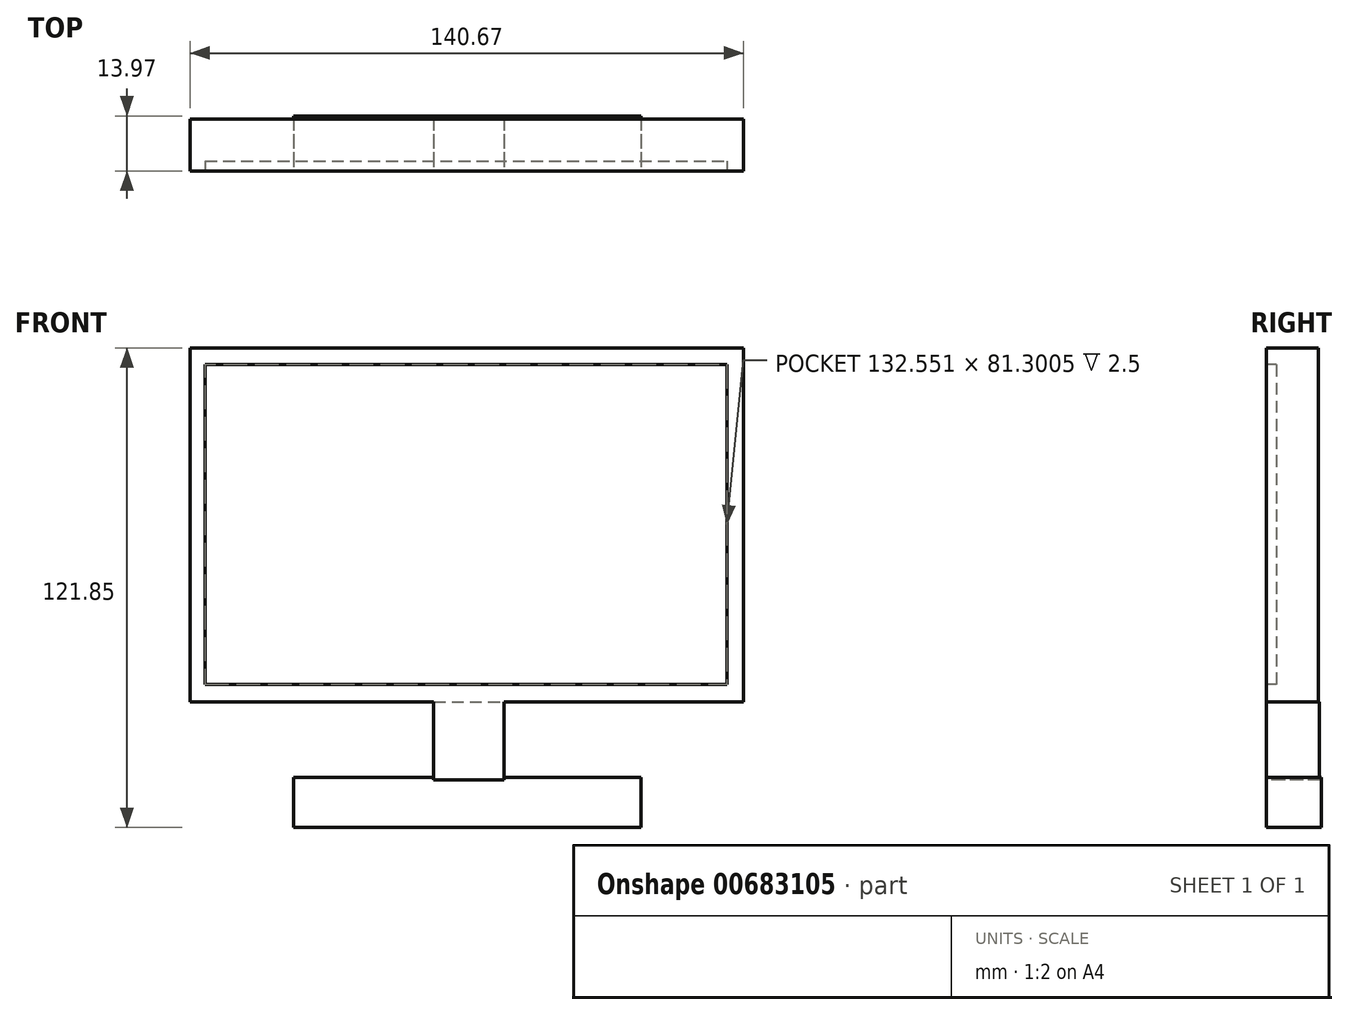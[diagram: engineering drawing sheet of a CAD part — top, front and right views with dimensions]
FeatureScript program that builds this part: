
annotation { "Feature Type Name" : "Feature", "Feature Type Description" : "" }
export const myFeature = defineFeature(function(context is Context, id is Id, definition is map)
    precondition{}
    {
        {
            var Q0;
            Q0=qCreatedBy(makeId("Front.planeOp"),FACE);
            var sketch = newSketch(context, id + "F0", { "sketchPlane" : qUnion([Q0])});
            skLineSegment(sketch, "E0.bottom", {"start": v(-71.8, 53.92) * mm, "end": v(68.86, 53.92) * mm});
            skLineSegment(sketch, "E0.top", {"start": v(-71.8, -36.04) * mm, "end": v(68.86, -36.04) * mm});
            skLineSegment(sketch, "E0.left", {"start": v(-71.8, 53.92) * mm, "end": v(-71.8, -36.04) * mm});
            skLineSegment(sketch, "E0.right", {"start": v(68.86, 53.92) * mm, "end": v(68.86, -36.04) * mm});
            skSolve(sketch);
        }
        {
            var Q0;
            Q0=makeQuery(id+"F0.imprint","IMPRINT",FACE,{"disambiguationData":[TD([[makeQuery(id+"F0.imprint","IMPRINT",EDGE,{"derivedFrom":sQuery(id+"F0.wireOp",EDGE,"E0.bottom")}),-1.0]])]});
            extrude(context, id + "F1", {"entities" : qUnion([Q0]), "depth" : 13.2 * mm, "offsetDistance" : 25.4 * mm});
        }
        {
            var Q0;
            Q0=makeQuery(id+"F1.opExtrude","CAP_FACE",FACE,{"disambiguationData":[OSD([sQuery(id+"F0.wireOp",EDGE,"E0.bottom"),sQuery(id+"F0.wireOp",EDGE,"E0.top"),sQuery(id+"F0.wireOp",EDGE,"E0.left"),sQuery(id+"F0.wireOp",EDGE,"E0.right")])],"isStart":false});
            var sketch = newSketch(context, id + "F2", { "sketchPlane" : qUnion([Q0])});
            skLineSegment(sketch, "E1.bottom", {"start": v(-67.93, 49.68) * mm, "end": v(64.62, 49.68) * mm});
            skLineSegment(sketch, "E1.top", {"start": v(-67.93, -31.62) * mm, "end": v(64.62, -31.62) * mm});
            skLineSegment(sketch, "E1.left", {"start": v(-67.93, 49.68) * mm, "end": v(-67.93, -31.62) * mm});
            skLineSegment(sketch, "E1.right", {"start": v(64.62, 49.68) * mm, "end": v(64.62, -31.62) * mm});
            skSolve(sketch);
        }
        {
            var Q0;
            Q0 = qSketchRegion(id + "F2", true);
            extrude(context, id + "F3", {"entities" : qUnion([Q0]), "operationType" : NewBodyOperationType.REMOVE, "endBound" : BoundingType.SYMMETRIC, "oppositeDirection" : true, "depth" : 10 * mm, "offsetDistance" : 25.4 * mm});
        }
        {
            var Q0;
            Q0=makeQuery(id+"F3.boolean.opBoolean","COPY",FACE,{"derivedFrom":makeQuery(id+"F3.opExtrude","CAP_FACE",FACE,{"disambiguationData":[OSD([sQuery(id+"F2.wireOp",EDGE,"E1.bottom"),sQuery(id+"F2.wireOp",EDGE,"E1.top"),sQuery(id+"F2.wireOp",EDGE,"E1.left"),sQuery(id+"F2.wireOp",EDGE,"E1.right")])],"isStart":false})});
            var sketch = newSketch(context, id + "F4", { "sketchPlane" : qUnion([Q0])});
            skLineSegment(sketch, "E2.bottom", {"start": v(-67.93, 49.68) * mm, "end": v(64.62, 49.68) * mm});
            skLineSegment(sketch, "E2.top", {"start": v(-67.93, -31.62) * mm, "end": v(64.62, -31.62) * mm});
            skLineSegment(sketch, "E2.left", {"start": v(-67.93, 49.68) * mm, "end": v(-67.93, -31.62) * mm});
            skLineSegment(sketch, "E2.right", {"start": v(64.62, 49.68) * mm, "end": v(64.62, -31.62) * mm});
            skSolve(sketch);
        }
        {
            var Q0;
            Q0 = qSketchRegion(id + "F4", true);
            extrude(context, id + "F5", {"entities" : qUnion([Q0]), "operationType" : NewBodyOperationType.ADD, "depth" : 2.5 * mm, "offsetDistance" : 25.4 * mm});
        }
        {
            var Q0;
            Q0=makeQuery(id+"F1.opExtrude","CAP_FACE",FACE,{"disambiguationData":[OSD([sQuery(id+"F0.wireOp",EDGE,"E0.bottom"),sQuery(id+"F0.wireOp",EDGE,"E0.top"),sQuery(id+"F0.wireOp",EDGE,"E0.left"),sQuery(id+"F0.wireOp",EDGE,"E0.right")])],"isStart":false});
            var sketch = newSketch(context, id + "F6", { "sketchPlane" : qUnion([Q0])});
            skLineSegment(sketch, "E3.bottom", {"start": v(-9.86, -36.04) * mm, "end": v(8.02, -36.04) * mm});
            skLineSegment(sketch, "E3.top", {"start": v(-9.86, -55.77) * mm, "end": v(8.02, -55.77) * mm});
            skLineSegment(sketch, "E3.left", {"start": v(-9.86, -36.04) * mm, "end": v(-9.86, -55.77) * mm});
            skLineSegment(sketch, "E3.right", {"start": v(8.02, -36.04) * mm, "end": v(8.02, -55.77) * mm});
            skSolve(sketch);
        }
        {
            var Q0;
            Q0 = qSketchRegion(id + "F6", true);
            extrude(context, id + "F7", {"entities" : qUnion([Q0]), "operationType" : NewBodyOperationType.ADD, "oppositeDirection" : true, "depth" : 13.46 * mm, "offsetDistance" : 25.4 * mm});
        }
        {
            var Q0;
            Q0=makeQuery(id+"F7.boolean.opBoolean","MERGE",FACE,{"derivedFrom":[makeQuery(id+"F1.opExtrude","CAP_FACE",FACE,{"disambiguationData":[OSD([sQuery(id+"F0.wireOp",EDGE,"E0.bottom"),sQuery(id+"F0.wireOp",EDGE,"E0.top"),sQuery(id+"F0.wireOp",EDGE,"E0.left"),sQuery(id+"F0.wireOp",EDGE,"E0.right")])],"isStart":false}),makeQuery(id+"F7.opExtrude","CAP_FACE",FACE,{"disambiguationData":[OSD([sQuery(id+"F6.wireOp",EDGE,"E3.bottom"),sQuery(id+"F6.wireOp",EDGE,"E3.top"),sQuery(id+"F6.wireOp",EDGE,"E3.left"),sQuery(id+"F6.wireOp",EDGE,"E3.right")])],"isStart":true})]});
            var sketch = newSketch(context, id + "F8", { "sketchPlane" : qUnion([Q0])});
            skSolve(sketch);
        }
        {
            var Q0;
            {var subQ6=sQuery(id+"F0.wireOp",EDGE,"E0.bottom");Q0=makeQuery(id+"F8.imprint","IMPRINT",FACE,{"disambiguationData":[TD([[makeQuery(id+"F8.imprint","IMPRINT",EDGE,{"derivedFrom":makeQuery(id+"F1.opExtrude","CAP_EDGE",EDGE,{"disambiguationData":[OSD([subQ6])],"isStart":false})}),-1.0]])]});}
            var sketch = newSketch(context, id + "F9", { "sketchPlane" : qUnion([Q0])});
            skLineSegment(sketch, "E4", {"start": v(-9.86, -55.21) * mm, "end": v(-45.44, -55.21) * mm});
            skLineSegment(sketch, "E5", {"start": v(-45.44, -55.21) * mm, "end": v(-45.44, -67.93) * mm});
            skLineSegment(sketch, "E6", {"start": v(-45.44, -67.93) * mm, "end": v(42.86, -67.93) * mm});
            skLineSegment(sketch, "E7", {"start": v(42.86, -67.93) * mm, "end": v(42.86, -55.21) * mm});
            skLineSegment(sketch, "E8", {"start": v(42.86, -55.21) * mm, "end": v(7.65, -55.21) * mm});
            skSolve(sketch);
        }
        {
            var Q0;
            {var subQ2=sQuery(id+"F9.wireOp",EDGE,"E4");Q0=makeQuery(id+"F9.imprint","IMPRINT",FACE,{"disambiguationData":[TD([[makeQuery(id+"F9.imprint","IMPRINT",EDGE,{"derivedFrom":subQ2}),1.0]])]});}
            extrude(context, id + "F10", {"entities" : qUnion([Q0]), "oppositeDirection" : true, "depth" : 13.97 * mm, "offsetDistance" : 25.4 * mm});
        }
    });
